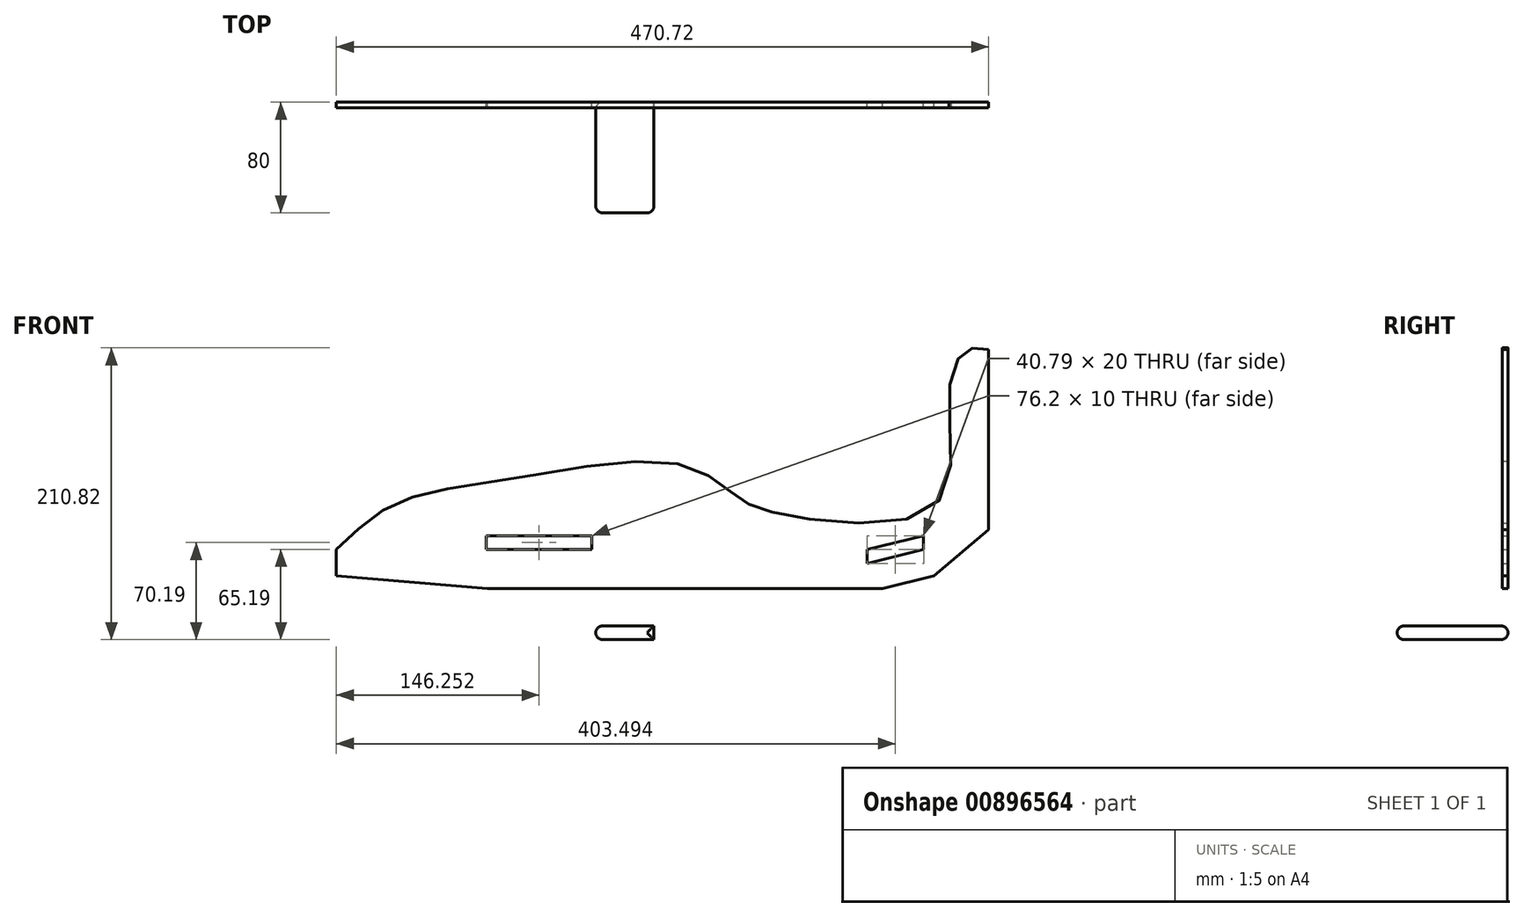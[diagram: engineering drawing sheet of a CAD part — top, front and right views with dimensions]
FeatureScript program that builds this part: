
annotation { "Feature Type Name" : "Feature", "Feature Type Description" : "" }
export const myFeature = defineFeature(function(context is Context, id is Id, definition is map)
    precondition{}
    {
        {
            var Q0;
            Q0=qCreatedBy(makeId("Front.planeOp"),FACE);
            var sketch = newSketch(context, id + "F0", { "sketchPlane" : qUnion([Q0])});
            skFitSpline(sketch, "E0", {"points": [v(-231.67, 0) * mm, v(-189.89, 32.57) * mm, v(-106.31, 51) * mm, v(19.05, 60.84) * mm, v(58.38, 37.49) * mm, v(91.56, 25.2) * mm, v(200.95, 32.57) * mm, v(210.78, 116.14) * mm, v(224.3, 144.41) * mm, v(239.05, 144.41) * mm], "startDerivative": vector(360.35, 353.76) * mm, "endDerivative": vector(275.67, -57.4) * mm});
            skLineSegment(sketch, "E1", {"start": v(239.05, 144.41) * mm, "end": v(239.05, 14.13) * mm});
            skLineSegment(sketch, "E2", {"start": v(239.05, 14.13) * mm, "end": v(199.72, -19.05) * mm});
            skLineSegment(sketch, "E3", {"start": v(199.72, -19.05) * mm, "end": v(162.66, -28.14) * mm});
            skLineSegment(sketch, "E4", {"start": v(162.66, -28.14) * mm, "end": v(127.01, -28.14) * mm});
            skLineSegment(sketch, "E5", {"start": v(127.01, -28.14) * mm, "end": v(-122.48, -28.14) * mm});
            skLineSegment(sketch, "E6", {"start": v(-122.48, -28.14) * mm, "end": v(-231.67, -19.05) * mm});
            skLineSegment(sketch, "E7", {"start": v(-231.67, -19.05) * mm, "end": v(-231.67, 0) * mm});
            skLineSegment(sketch, "E8.bottom", {"start": v(-123.52, 0) * mm, "end": v(-47.32, 0) * mm});
            skLineSegment(sketch, "E8.top", {"start": v(-123.52, 10) * mm, "end": v(-47.32, 10) * mm});
            skLineSegment(sketch, "E8.left", {"start": v(-123.52, 0) * mm, "end": v(-123.52, 10) * mm});
            skLineSegment(sketch, "E8.right", {"start": v(-47.32, 0) * mm, "end": v(-47.32, 10) * mm});
            skLineSegment(sketch, "E9", {"start": v(151.43, 0) * mm, "end": v(192.22, 10) * mm});
            skLineSegment(sketch, "E10", {"start": v(192.22, 0) * mm, "end": v(192.22, 10) * mm});
            skLineSegment(sketch, "E11", {"start": v(151.43, 0) * mm, "end": v(151.43, -10) * mm});
            skLineSegment(sketch, "E12", {"start": v(151.43, -10) * mm, "end": v(192.22, 0) * mm});
            skSolve(sketch);
        }
        {
            var Q0;
            Q0=makeQuery(id+"F0.imprint","IMPRINT",FACE,{"disambiguationData":[TD([[makeQuery(id+"F0.imprint","IMPRINT",EDGE,{"derivedFrom":sQuery(id+"F0.wireOp",EDGE,"E0")}),-1.0]])]});
            extrude(context, id + "F1", {"entities" : qUnion([Q0]), "depth" : 4 * mm, "offsetDistance" : 25 * mm});
        }
        {
            var Q0;
            Q0=qCreatedBy(makeId("Front.planeOp"),FACE);
            var sketch = newSketch(context, id + "F2", { "sketchPlane" : qUnion([Q0])});
            skLineSegment(sketch, "E13.bottom", {"start": v(-44.47, -55.2) * mm, "end": v(-2.47, -55.2) * mm});
            skLineSegment(sketch, "E13.top", {"start": v(-44.47, -65.2) * mm, "end": v(-2.47, -65.2) * mm});
            skLineSegment(sketch, "E13.left", {"start": v(-44.47, -55.2) * mm, "end": v(-44.47, -65.2) * mm});
            skLineSegment(sketch, "E13.right", {"start": v(-2.47, -55.2) * mm, "end": v(-2.47, -65.2) * mm});
            skSolve(sketch);
        }
        {
            var Q0;
            Q0 = qSketchRegion(id + "F2", true);
            extrude(context, id + "F3", {"entities" : qUnion([Q0]), "depth" : 80 * mm, "offsetDistance" : 25 * mm});
        }
        {
            var Q0;
            Q0=makeQuery(id+"F3.opExtrude","SWEPT_EDGE",EDGE,{"disambiguationData":[OSD([sQuery(id+"F2.wireOp",EDGE,"E13.bottom"),sQuery(id+"F2.wireOp",EDGE,"E13.left")])]});
            var Q1;
            Q1=makeQuery(id+"F3.opExtrude","SWEPT_EDGE",EDGE,{"disambiguationData":[OSD([sQuery(id+"F2.wireOp",EDGE,"E13.top"),sQuery(id+"F2.wireOp",EDGE,"E13.left")])]});
            var Q2;
            Q2=makeQuery(id+"F3.opExtrude","CAP_EDGE",EDGE,{"disambiguationData":[OSD([sQuery(id+"F2.wireOp",EDGE,"E13.left")])],"isStart":false});
            var Q3;
            Q3=makeQuery(id+"F3.opExtrude","CAP_EDGE",EDGE,{"disambiguationData":[OSD([sQuery(id+"F2.wireOp",EDGE,"E13.left")])],"isStart":true});
            var Q4;
            Q4=makeQuery(id+"F3.opExtrude","CAP_FACE",FACE,{"disambiguationData":[OSD([sQuery(id+"F2.wireOp",EDGE,"E13.bottom"),sQuery(id+"F2.wireOp",EDGE,"E13.top"),sQuery(id+"F2.wireOp",EDGE,"E13.left"),sQuery(id+"F2.wireOp",EDGE,"E13.right")])],"isStart":false});
            var Q5;
            Q5=makeQuery(id+"F3.opExtrude","CAP_EDGE",EDGE,{"disambiguationData":[OSD([sQuery(id+"F2.wireOp",EDGE,"E13.top")])],"isStart":false});
            var Q6;
            Q6=makeQuery(id+"F3.opExtrude","CAP_EDGE",EDGE,{"disambiguationData":[OSD([sQuery(id+"F2.wireOp",EDGE,"E13.bottom")])],"isStart":true});
            var Q7;
            Q7=makeQuery(id+"F3.opExtrude","CAP_EDGE",EDGE,{"disambiguationData":[OSD([sQuery(id+"F2.wireOp",EDGE,"E13.top")])],"isStart":true});
            fillet(context, id + "F4", {"entities" : qUnion([Q0, Q1, Q2, Q3, Q4, Q5, Q6, Q7]), "radius" : 5 * mm, "tangentPropagation" : true, "allowEdgeOverflow" : false});
        }
    });
